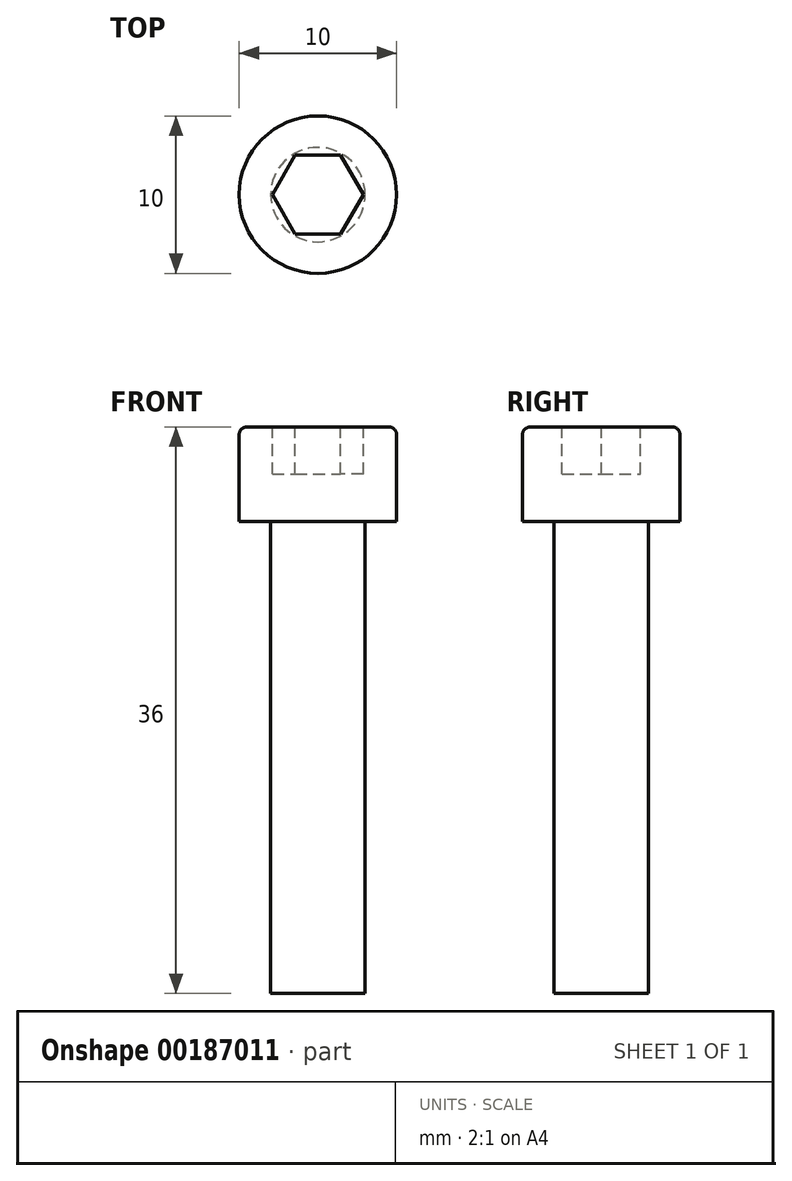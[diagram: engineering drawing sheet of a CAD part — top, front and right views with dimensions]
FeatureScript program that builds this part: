
annotation { "Feature Type Name" : "Feature", "Feature Type Description" : "" }
export const myFeature = defineFeature(function(context is Context, id is Id, definition is map)
    precondition{}
    {
        {
            var Q0;
            Q0=qCreatedBy(makeId("Front.planeOp"),FACE);
            var sketch = newSketch(context, id + "F0", { "sketchPlane" : qUnion([Q0])});
            skLineSegment(sketch, "E0", {"start": v(0, -30) * mm, "end": v(-3, -30) * mm});
            skLineSegment(sketch, "E1", {"start": v(-3, -30) * mm, "end": v(-3, 0) * mm});
            skLineSegment(sketch, "E2", {"start": v(-3, 0) * mm, "end": v(-5, 0) * mm});
            skLineSegment(sketch, "E3", {"start": v(-5, 0) * mm, "end": v(-5, 6) * mm});
            skLineSegment(sketch, "E4", {"start": v(-5, 6) * mm, "end": v(0, 6) * mm});
            skLineSegment(sketch, "E5", {"start": v(0, 6) * mm, "end": v(0, -30) * mm});
            skSolve(sketch);
        }
        {
            var Q0;
            Q0=makeQuery(id+"F0.imprint","IMPRINT",FACE,{"disambiguationData":[TD([[makeQuery(id+"F0.imprint","IMPRINT",EDGE,{"derivedFrom":sQuery(id+"F0.wireOp",EDGE,"E0")}),-1.0]])]});
            var Q1;
            Q1=sQuery(id+"F0.wireOp",EDGE,"E5");
            revolve(context, id + "F1", {"entities" : qUnion([Q0]), "axis" : qUnion([Q1]), "revolveType" : RevolveType.FULL});
        }
        {
            var Q0;
            Q0=makeQuery(id+"F1.opRevolve","SWEPT_FACE",FACE,{"disambiguationData":[OSD([sQuery(id+"F0.wireOp",EDGE,"E4")])]});
            var sketch = newSketch(context, id + "F2", { "sketchPlane" : qUnion([Q0])});
            skCircle(sketch, "E6.cCircle", {"center": v(0, 0) * mm, "radius": 2.5 * mm, "construction": true});
            skLineSegment(sketch, "E6.0", {"start": v(-1.44, 2.5) * mm, "end": v(1.44, 2.5) * mm});
            skLineSegment(sketch, "E6.1", {"start": v(1.44, 2.5) * mm, "end": v(2.89, 0) * mm});
            skLineSegment(sketch, "E6.2", {"start": v(2.89, 0) * mm, "end": v(1.44, -2.5) * mm});
            skLineSegment(sketch, "E6.3", {"start": v(1.44, -2.5) * mm, "end": v(-1.44, -2.5) * mm});
            skLineSegment(sketch, "E6.4", {"start": v(-1.44, -2.5) * mm, "end": v(-2.89, 0) * mm});
            skLineSegment(sketch, "E6.5", {"start": v(-2.89, 0) * mm, "end": v(-1.44, 2.5) * mm});
            skPoint(sketch, "E6.0.midPoint", {"position": v(0, 2.5) * mm});
            skSolve(sketch);
        }
        {
            var Q0;
            Q0=qSketchRegion(id+"F2",true);
            extrude(context, id + "F3", {"entities" : qUnion([Q0]), "operationType" : NewBodyOperationType.REMOVE, "oppositeDirection" : true, "depth" : 3 * mm});
        }
        {
            var Q0;
            Q0=makeQuery(id+"F1.opRevolve","SWEPT_EDGE",EDGE,{"disambiguationData":[OSD([sQuery(id+"F0.wireOp",EDGE,"E3"),sQuery(id+"F0.wireOp",EDGE,"E4")])]});
            fillet(context, id + "F4", {"entities" : qUnion([Q0]), "radius" : .5 * mm, "tangentPropagation" : true, "allowEdgeOverflow" : false});
        }
    });
